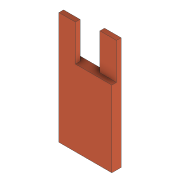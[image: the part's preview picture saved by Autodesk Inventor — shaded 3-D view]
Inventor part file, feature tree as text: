
AUTODESK INVENTOR PART (.ipt)
format: ipt  version: 2021 (Build 250183000, 183)  size: 111,616 bytes
history: native  units: in
note: dims shown in document units (in); Inventor stores cm internally (conversion verified against a paired STEP export)
features: extrude x4, sketch x4
ambient origin geometry x8: Origin, YZ Plane, XZ Plane, XY Plane, X Axis, Y Axis, Z Axis, Center Point
bodies: Solid1 (feature_tree)
feature tree (8):
  extrude  "Extrusion1"  Depth=0.6693in
  extrude  "Extrusion2"  Depth=0.1181in
  extrude  "Extrusion3"  Depth=0.0984in
  extrude  "Extrusion4"  Depth=0.2165in
  sketch  "Sketch1"  dims[d0=0.315in d1=0.6693in]
  sketch  "Sketch2"  dims[d2=0.0551in d3=0.0in d4=0.1181in]
  sketch  "Sketch3"  dims[d5=0.2165in d6=0.0984in]
  sketch  "Sketch4"  dims[d7=0.0551in d8=0.0in d9=0.2165in d10=0.0276in d11=0.0in d12=0.0276in d13=0.0in d14=0.0197in d15=0.0344in]
